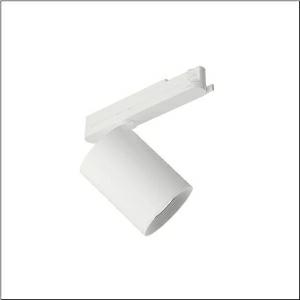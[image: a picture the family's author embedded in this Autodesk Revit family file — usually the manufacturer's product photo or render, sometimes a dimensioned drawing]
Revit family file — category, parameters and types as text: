
# Revit family: spot_21_51se12mba5b
name_source: partatom
category: Lighting Fixtures
units: mm (PartAtom-declared; Revit-internal decimal feet)

## family parameters
Cut with Voids When Loaded = No
Host = Face
Light Source = No
Part Type = Normal
Room Calculation Point = No
Round Connector Dimension = Use Diameter
Shared = No

## types (1)
- --- (1 x LED, 5240 lm, 41.7 W, 2700K)
    Apparent Load = 42 VA
    CIE Flux Codes = 95 98 99 100 100
    Color Rendering = 90
    Color Temperature = 2700K
    Default Elevation = 1800 mm
    Description = Spot 21, directional spotlight, light control with lens, of PMMA, LED rated luminous flux: 5.040lm, light colour: 927, control gear: ECG Multilumen, with 3-phase adapter, mains connection: 220..240V, AC, 50/60Hz, of aluminium, traffic white (RAL 9016), length: 213mm, diameter: 105mm, protection rating (complete): IP20, insulation class (complete): insulation class I (protective earthing), certification: CE, impact resistance: IK02, permissible ambient temperature for indoor applications: -20..+40°C, packaging unit: 1 piece
    Height = 175 mm
    Lamp = 1 x LED
    Lamp Light Flux = 5240 lm
    Lamp Power = 41.7 W
    Lamp count = 1
    Length = 105 mm
    Luminous efficacy = 126 lm/W
    Manufacturer = Siteco
    ModVariant = No
    Model = 51SE12MBA5B
    Mounting Place = Ceiling
    Mounting Type = Pendant
    Number of Poles = 1
    OnlyDefault = Yes
    Power Factor = 1
    Product Name = Spot 21
    Product group = directional spotlight
    ProductGroupID = 904
    Protection Class = Protection class I
    Protection Degree = IP 20
    RLX_Detail_Level = 1
    RlxData = <blob elided: 17649 chars, md5=cb3e852f>
    Socket = socket
    Standby Power = 0 W
    System Light Flux = 5240 lm
    System Power = 42 W
    Type Comments = factory setting: luminous flux: 100 % | (ON | ON | ON | ON) | 1050 mA
    Type Image = l_1003976.jpg
    URL = http://relux.com
    VarID = @adj_053693
    Voltage = 0 V
    Weight = 0.00 kg
    Width = 0 mm  [stored 0 ft]

note: [stored X ft] marks values corroborated as IEEE doubles in the binary element streams (Revit-internal decimal feet)

## geometry (parser evidence)
native form markers: Blend x4, Sweep x11
no freeform markers — native parametric forms only
